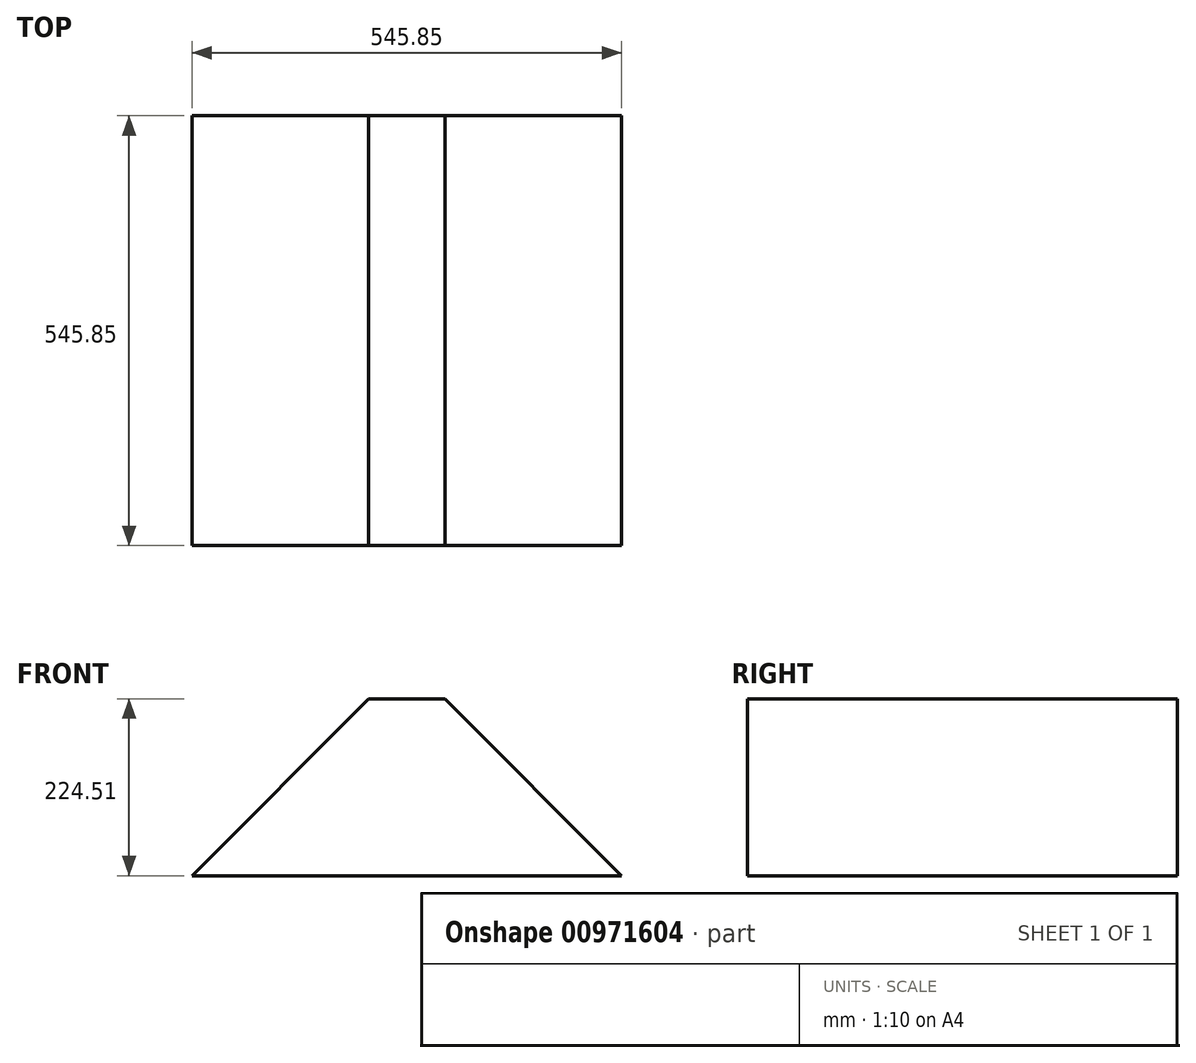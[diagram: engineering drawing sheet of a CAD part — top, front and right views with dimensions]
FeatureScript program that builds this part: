
annotation { "Feature Type Name" : "Feature", "Feature Type Description" : "" }
export const myFeature = defineFeature(function(context is Context, id is Id, definition is map)
    precondition{}
    {
        {
            var Q0;
            Q0=qCreatedBy(makeId("Front.planeOp"),FACE);
            var sketch = newSketch(context, id + "F0", { "sketchPlane" : qUnion([Q0])});
            skLineSegment(sketch, "E0", {"start": v(-268.5, -202.08) * mm, "end": v(277.35, -202.08) * mm});
            skLineSegment(sketch, "E1", {"start": v(277.35, -202.08) * mm, "end": v(52.84, 22.43) * mm});
            skLineSegment(sketch, "E2", {"start": v(52.84, 22.43) * mm, "end": v(-43.99, 22.43) * mm});
            skLineSegment(sketch, "E3", {"start": v(-43.99, 22.43) * mm, "end": v(-268.5, -202.08) * mm});
            skSolve(sketch);
        }
        {
            var Q0;
            Q0=makeQuery(id+"F0.imprint","IMPRINT",FACE,{"disambiguationData":[TD([[makeQuery(id+"F0.imprint","IMPRINT",EDGE,{"derivedFrom":sQuery(id+"F0.wireOp",EDGE,"E0")}),1.0]])]});
            extrude(context, id + "F1", {"entities" : qUnion([Q0]), "depth" : 545.85 * mm, "offsetDistance" : 25.4 * mm});
        }
    });
